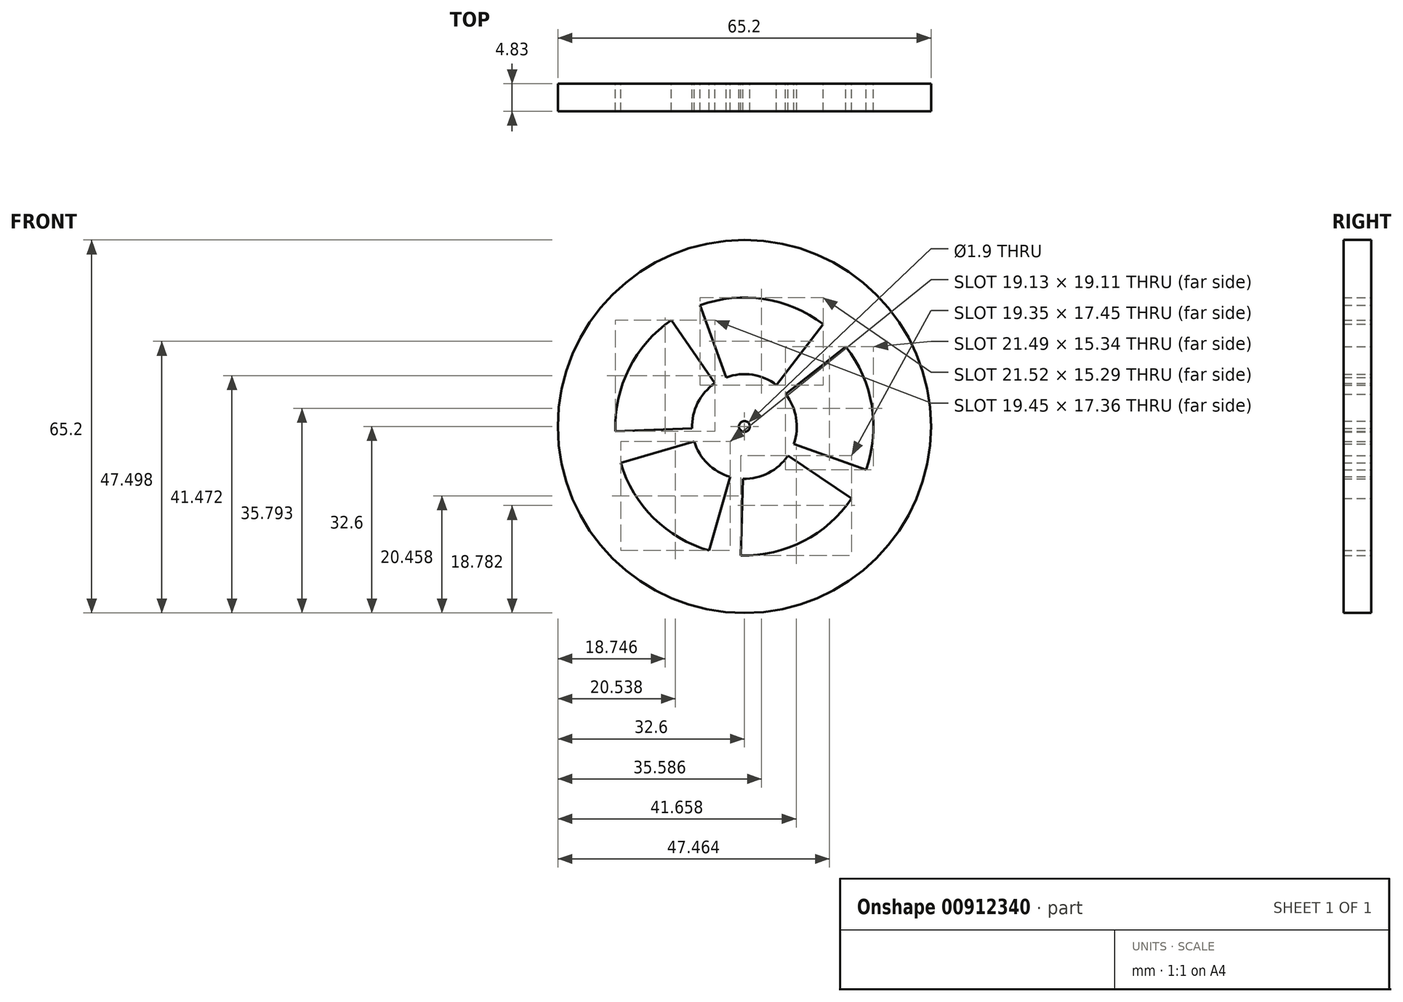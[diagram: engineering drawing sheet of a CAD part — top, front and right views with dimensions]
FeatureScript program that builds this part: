
annotation { "Feature Type Name" : "Feature", "Feature Type Description" : "" }
export const myFeature = defineFeature(function(context is Context, id is Id, definition is map)
    precondition{}
    {
        {
            var Q0;
            Q0=qCreatedBy(makeId("Front.planeOp"),FACE);
            var sketch = newSketch(context, id + "F0", { "sketchPlane" : qUnion([Q0])});
            skArc(sketch, "E0", {"start": v(-5.17, 7.55) * mm, "mid": v(-8.17, 4.11) * mm, "end": v(-9.14, -0.35) * mm});
            skArc(sketch, "E1", {"start": v(-12.75, 18.6) * mm, "mid": v(-20.15, 10.13) * mm, "end": v(-22.53, -0.85) * mm});
            skLineSegment(sketch, "E2", {"start": v(-12.75, 18.6) * mm, "end": v(-5.17, 7.55) * mm});
            skLineSegment(sketch, "E3", {"start": v(-7.78, 21.17) * mm, "end": v(-3.16, 8.59) * mm});
            skCircle(sketch, "E4", {"center": v(0, 0) * mm, "radius": 32.6 * mm});
            skLineSegment(sketch, "E5.1.0", {"start": v(-21.63, -6.38) * mm, "end": v(-8.78, -2.59) * mm});
            skLineSegment(sketch, "E5.1.1", {"start": v(-22.53, -0.85) * mm, "end": v(-9.14, -0.35) * mm});
            skLineSegment(sketch, "E5.2.0", {"start": v(-0.62, -22.54) * mm, "end": v(-0.25, -9.15) * mm});
            skLineSegment(sketch, "E5.2.1", {"start": v(-6.15, -21.7) * mm, "end": v(-2.5, -8.8) * mm});
            skLineSegment(sketch, "E5.3.0", {"start": v(21.25, -7.55) * mm, "end": v(8.62, -3.06) * mm});
            skLineSegment(sketch, "E5.3.1", {"start": v(18.73, -12.55) * mm, "end": v(7.6, -5.1) * mm});
            skLineSegment(sketch, "E5.4.0", {"start": v(13.75, 17.87) * mm, "end": v(5.58, 7.25) * mm});
            skLineSegment(sketch, "E5.4.1", {"start": v(17.73, 13.94) * mm, "end": v(7.2, 5.65) * mm});
            skArc(sketch, "E6.trimOffspring", {"start": v(-8.78, -2.59) * mm, "mid": v(-6.44, -6.5) * mm, "end": v(-2.5, -8.8) * mm});
            skArc(sketch, "E7.trimOffspring", {"start": v(-0.25, -9.15) * mm, "mid": v(4.2, -8.13) * mm, "end": v(7.6, -5.1) * mm});
            skArc(sketch, "E8.trimOffspring", {"start": v(8.62, -3.06) * mm, "mid": v(9.03, 1.48) * mm, "end": v(7.2, 5.65) * mm});
            skArc(sketch, "E9.trimOffspring", {"start": v(5.58, 7.25) * mm, "mid": v(1.38, 9.04) * mm, "end": v(-3.16, 8.59) * mm});
            skArc(sketch, "E10.trimOffspring", {"start": v(13.75, 17.87) * mm, "mid": v(3.4, 22.3) * mm, "end": v(-7.78, 21.17) * mm});
            skArc(sketch, "E11.trimOffspring", {"start": v(21.25, -7.55) * mm, "mid": v(22.25, 3.65) * mm, "end": v(17.73, 13.94) * mm});
            skArc(sketch, "E12.trimOffspring", {"start": v(-0.62, -22.54) * mm, "mid": v(10.34, -20.04) * mm, "end": v(18.73, -12.55) * mm});
            skArc(sketch, "E13.trimOffspring", {"start": v(-21.63, -6.38) * mm, "mid": v(-15.86, -16.03) * mm, "end": v(-6.15, -21.7) * mm});
            skSolve(sketch);
        }
        {
            var Q0;
            Q0=makeQuery(id+"F0.imprint","IMPRINT",FACE,{"disambiguationData":[TD([[makeQuery(id+"F0.imprint","IMPRINT",EDGE,{"derivedFrom":sQuery(id+"F0.wireOp",EDGE,"E4")}),1.0]])]});
            var Q1;
            {var subQ0=sQuery(id+"F0.wireOp",EDGE,"E2");Q1=makeQuery(id+"F0.imprint","IMPRINT",FACE,{"disambiguationData":[TD([[makeQuery(id+"F0.imprint","IMPRINT",EDGE,{"derivedFrom":subQ0}),1.0]])]});}
            var Q2;
            {var subQ0=sQuery(id+"F0.wireOp",EDGE,"E5.4.0");Q2=makeQuery(id+"F0.imprint","IMPRINT",FACE,{"disambiguationData":[TD([[makeQuery(id+"F0.imprint","IMPRINT",EDGE,{"derivedFrom":subQ0}),1.0]])]});}
            var Q3;
            {var subQ0=sQuery(id+"F0.wireOp",EDGE,"E5.3.0");Q3=makeQuery(id+"F0.imprint","IMPRINT",FACE,{"disambiguationData":[TD([[makeQuery(id+"F0.imprint","IMPRINT",EDGE,{"derivedFrom":subQ0}),1.0]])]});}
            var Q4;
            {var subQ0=sQuery(id+"F0.wireOp",EDGE,"E5.2.0");Q4=makeQuery(id+"F0.imprint","IMPRINT",FACE,{"disambiguationData":[TD([[makeQuery(id+"F0.imprint","IMPRINT",EDGE,{"derivedFrom":subQ0}),1.0]])]});}
            var Q5;
            {var subQ0=sQuery(id+"F0.wireOp",EDGE,"E5.1.0");Q5=makeQuery(id+"F0.imprint","IMPRINT",FACE,{"disambiguationData":[TD([[makeQuery(id+"F0.imprint","IMPRINT",EDGE,{"derivedFrom":subQ0}),1.0]])]});}
            var Q6;
            Q6=makeQuery(id+"F0.imprint","IMPRINT",FACE,{"disambiguationData":[TD([[makeQuery(id+"F0.imprint","IMPRINT",EDGE,{"derivedFrom":sQuery(id+"F0.wireOp",EDGE,"lEbozs4r-N5fZ-wT8g-xHW1-bqn56I4drxfg")}),-1.0]])]});
            var Q7;
            Q7=makeQuery(id+"F0.imprint","IMPRINT",FACE,{"disambiguationData":[TD([[makeQuery(id+"F0.imprint","IMPRINT",EDGE,{"derivedFrom":sQuery(id+"F0.wireOp",EDGE,"lEbozs4r-N5fZ-wT8g-xHW1-bqn56I4drxfg")}),1.0]])]});
            extrude(context, id + "F1", {"entities" : qUnion([Q0, Q1, Q2, Q3, Q4, Q5, Q6, Q7]), "depth" : 4.83 * mm, "offsetDistance" : 25 * mm});
        }
        {
            var Q0;
            Q0=qCreatedBy(makeId("Front.planeOp"),FACE);
            var sketch = newSketch(context, id + "F2", { "sketchPlane" : qUnion([Q0])});
            skCircle(sketch, "E14", {"center": v(0, 0) * mm, "radius": 2.45 * mm});
            skLineSegment(sketch, "E15", {"start": v(17.72, 13.94) * mm, "end": v(7.19, 5.66) * mm});
            skLineSegment(sketch, "E16", {"start": v(5.59, 7.27) * mm, "end": v(13.73, 17.89) * mm});
            skFitSpline(sketch, "E17", {"points": [v(13.73, 17.89) * mm, v(17.72, 13.94) * mm], "startDerivative": vector(4.8, -3.62) * mm, "endDerivative": vector(3.17, -4.41) * mm});
            skFitSpline(sketch, "E18", {"points": [v(5.59, 7.27) * mm, v(7.19, 5.66) * mm], "startDerivative": vector(1.84, -1.08) * mm, "endDerivative": vector(1.29, -1.93) * mm});
            skSolve(sketch);
        }
        {
            var Q0;
            Q0=makeQuery(id+"F2.imprint","IMPRINT",FACE,{"disambiguationData":[TD([[makeQuery(id+"F2.imprint","IMPRINT",EDGE,{"derivedFrom":sQuery(id+"F2.wireOp",EDGE,"E14")}),1.0]])]});
            extrude(context, id + "F3", {"entities" : qUnion([Q0]), "operationType" : NewBodyOperationType.REMOVE, "endBound" : BoundingType.SYMMETRIC, "depth" : 50 * mm, "offsetDistance" : 25 * mm});
        }
        {
            var Q0;
            Q0=qCreatedBy(makeId("Front.planeOp"),FACE);
            var sketch = newSketch(context, id + "F4", { "sketchPlane" : qUnion([Q0])});
            skCircle(sketch, "E19", {"center": v(0, 0) * mm, "radius": 4.57 * mm});
            skSolve(sketch);
        }
        {
            var Q0;
            Q0=makeQuery(id+"F4.imprint","IMPRINT",FACE,{"disambiguationData":[TD([[makeQuery(id+"F4.imprint","IMPRINT",EDGE,{"derivedFrom":sQuery(id+"F4.wireOp",EDGE,"E19")}),1.0]])]});
            extrude(context, id + "F5", {"entities" : qUnion([Q0]), "operationType" : NewBodyOperationType.ADD, "depth" : 4.83 * mm, "offsetDistance" : 25 * mm});
        }
        {
            var Q0;
            Q0=makeQuery(id+"F5.boolean.opBoolean","MERGE",FACE,{"derivedFrom":[makeQuery(id+"F1.opExtrude","CAP_FACE",FACE,{"disambiguationData":[OSD([sQuery(id+"F0.wireOp",EDGE,"E0"),sQuery(id+"F0.wireOp",EDGE,"E1"),sQuery(id+"F0.wireOp",EDGE,"E2"),sQuery(id+"F0.wireOp",EDGE,"E3"),sQuery(id+"F0.wireOp",EDGE,"E4"),sQuery(id+"F0.wireOp",EDGE,"E5.1.0"),sQuery(id+"F0.wireOp",EDGE,"E5.1.1"),sQuery(id+"F0.wireOp",EDGE,"E5.2.0"),sQuery(id+"F0.wireOp",EDGE,"E5.2.1"),sQuery(id+"F0.wireOp",EDGE,"E5.3.0"),sQuery(id+"F0.wireOp",EDGE,"E5.3.1"),sQuery(id+"F0.wireOp",EDGE,"E5.4.0"),sQuery(id+"F0.wireOp",EDGE,"E5.4.1")])],"isStart":true}),makeQuery(id+"F5.opExtrude","CAP_FACE",FACE,{"disambiguationData":[OSD([sQuery(id+"F4.wireOp",EDGE,"E19")])],"isStart":true})]});
            var sketch = newSketch(context, id + "F6", { "sketchPlane" : qUnion([Q0])});
            skCircle(sketch, "E20", {"center": v(0, 0) * mm, "radius": 0.95 * mm});
            skSolve(sketch);
        }
        {
            var Q0;
            Q0=makeQuery(id+"F6.imprint","IMPRINT",FACE,{"disambiguationData":[TD([[makeQuery(id+"F6.imprint","IMPRINT",EDGE,{"derivedFrom":sQuery(id+"F6.wireOp",EDGE,"E20")}),1.0]])]});
            extrude(context, id + "F7", {"entities" : qUnion([Q0]), "operationType" : NewBodyOperationType.REMOVE, "oppositeDirection" : true, "depth" : 6.7 * mm, "offsetDistance" : 25 * mm});
        }
    });
